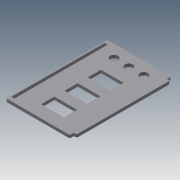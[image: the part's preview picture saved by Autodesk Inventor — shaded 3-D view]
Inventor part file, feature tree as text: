
AUTODESK INVENTOR PART (.ipt)
format: ipt  version: 2014 (Build 180170000, 170)  size: 145,920 bytes
history: native  units: mm
features: extrude x3, sketch x3, fillet x1
ambient origin geometry x8: Origin, YZ Plane, XZ Plane, XY Plane, X Axis, Y Axis, Z Axis, Center Point
bodies: Solid1 (feature_tree)
feature tree (7):
  extrude  "Extrusion1"  Depth=128.0mm
  extrude  "Extrusion2"  Depth=6.25mm
  fillet  "Fillet1"  Radius=2.875mm
  extrude  "Extrusion3"  Depth=8.0mm
  sketch  "Sketch1"  dims[d0=128.0mm d1=85.0mm]
  sketch  "Sketch2"  dims[d2=185.0mm d3=6.25mm d4=2.875mm]
  sketch  "Sketch3"  dims[d5=8.0mm d6=8.0mm d7=6.0mm d8=0.0mm d9=8.1mm d10=8.1mm d11=6.0mm d12=6.0mm d13=0.0mm d14=2.0mm d15=16.0mm d16=26.5mm d17=45.5mm d18=118.875mm d19=59.4375mm d20=30.0mm d21=30.0mm d22=25.0mm d23=25.0mm d24=10.0mm d25=0.0mm]
